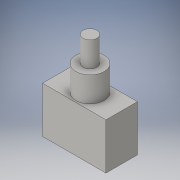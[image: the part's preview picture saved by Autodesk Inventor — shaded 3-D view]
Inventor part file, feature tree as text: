
AUTODESK INVENTOR PART (.ipt)
format: ipt  version: 2016 (Build 200138000, 138)  size: 109,568 bytes
history: native  units: in
note: dims shown in document units (in); Inventor stores cm internally (conversion verified against a paired STEP export)
features: extrude x3, sketch x3
ambient origin geometry x8: Origin, YZ Plane, XZ Plane, XY Plane, X Axis, Y Axis, Z Axis, Center Point
bodies: Solid1 (feature_tree)
feature tree (6):
  extrude  "Extrusion1"  Depth=0.367in
  extrude  "Extrusion2"  Depth=0.25in
  extrude  "Extrusion3"  Depth=0.2in
  sketch  "Sketch1"  dims[d0=0.504in d1=0.367in]
  sketch  "Sketch2"  dims[d2=0.25in d3=0.0in d4=0.225in]
  sketch  "Sketch3"  dims[d5=0.2in d6=0.0in d7=0.11in d8=0.2in d9=0.0in]
